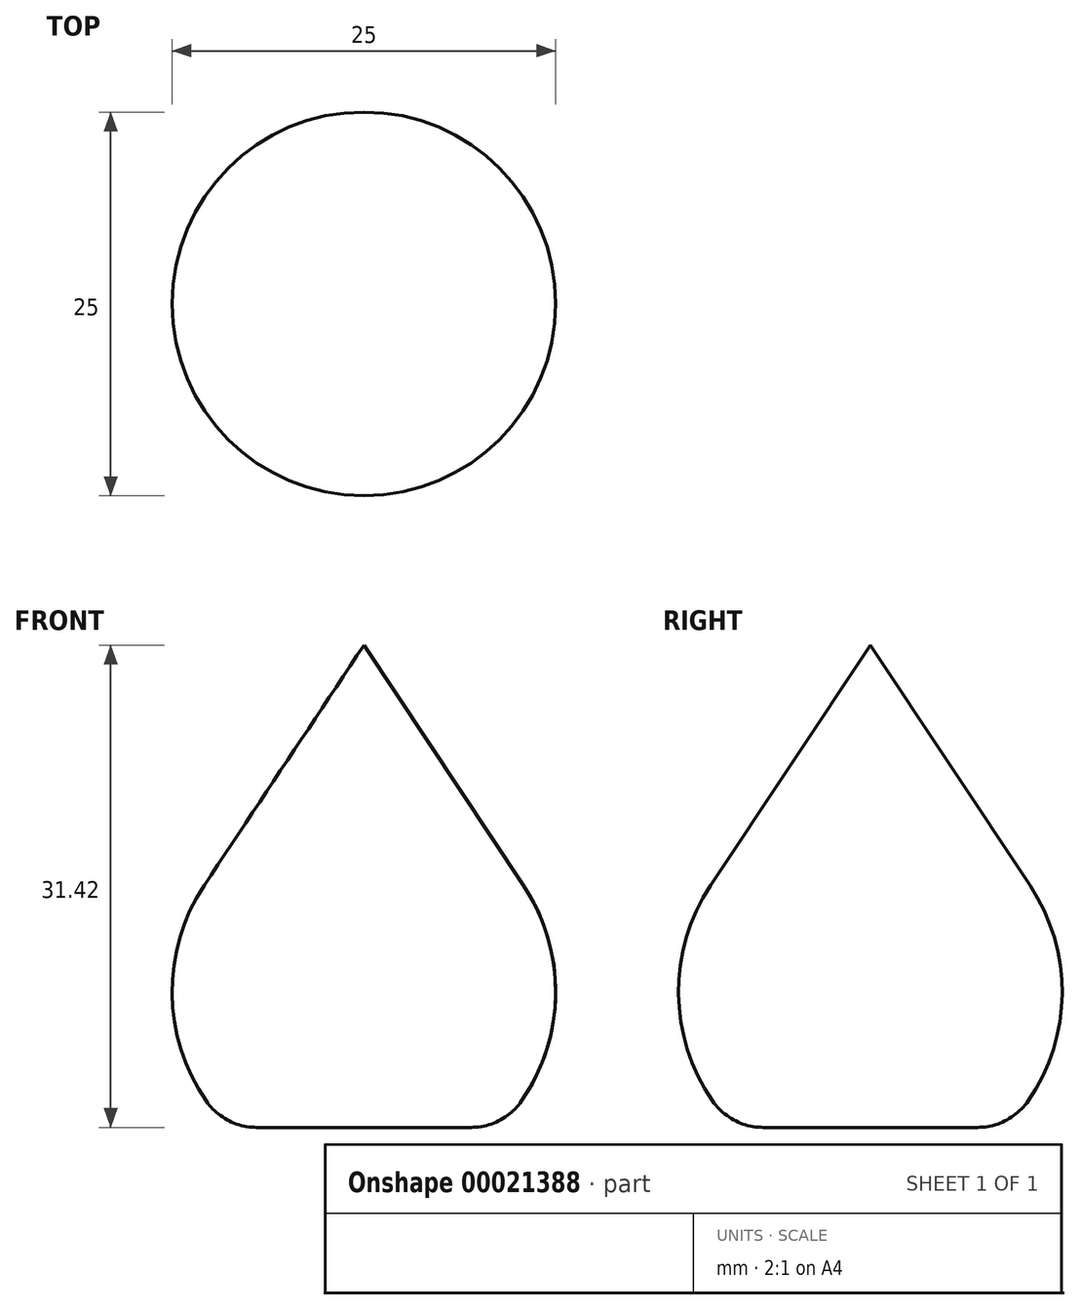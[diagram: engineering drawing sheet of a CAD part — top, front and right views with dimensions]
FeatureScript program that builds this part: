
annotation { "Feature Type Name" : "Feature", "Feature Type Description" : "" }
export const myFeature = defineFeature(function(context is Context, id is Id, definition is map)
    precondition{}
    {
        {
            var Q0;
            Q0=qCreatedBy(makeId("Front.planeOp"),FACE);
            var sketch = newSketch(context, id + "F0", { "sketchPlane" : qUnion([Q0])});
            skArc(sketch, "E0", {"start": v(-10.41, 6.92) * mm, "mid": v(-12.5, -0.12) * mm, "end": v(-10.28, -7.12) * mm});
            skLineSegment(sketch, "E1", {"start": v(0, 0) * mm, "end": v(-13.87, -13.87) * mm, "construction": true});
            skLineSegment(sketch, "E2", {"start": v(0, 43.33) * mm, "end": v(0, -25.95) * mm, "construction": true});
            skLineSegment(sketch, "E3", {"start": v(-6.99, -8.84) * mm, "end": v(0, -8.84) * mm});
            skPoint(sketch, "E4.visualSharp", {"position": v(-8.84, -8.84) * mm});
            skArc(sketch, "E4.filletArc", {"start": v(-10.28, -7.12) * mm, "mid": v(-8.84, -8.38) * mm, "end": v(-6.99, -8.84) * mm});
            skPoint(sketch, "E5.visualSharp", {"position": v(8.84, -8.84) * mm});
            skPoint(sketch, "E6.MirrorCS.end.orphan", {"position": v(13.87, -13.87) * mm});
            skLineSegment(sketch, "E7", {"start": v(0, 22.58) * mm, "end": v(-10.41, 6.92) * mm});
            skLineSegment(sketch, "E8", {"start": v(0, 22.58) * mm, "end": v(0, -8.84) * mm});
            skSolve(sketch);
        }
        {
            var Q0;
            Q0 = qSketchRegion(id + "F0", true);
            var Q1;
            Q1=sQuery(id+"F0.wireOp",EDGE,"E2");
            revolve(context, id + "F1", {"entities" : qUnion([Q0]), "axis" : qUnion([Q1]), "revolveType" : RevolveType.FULL});
        }
    });
